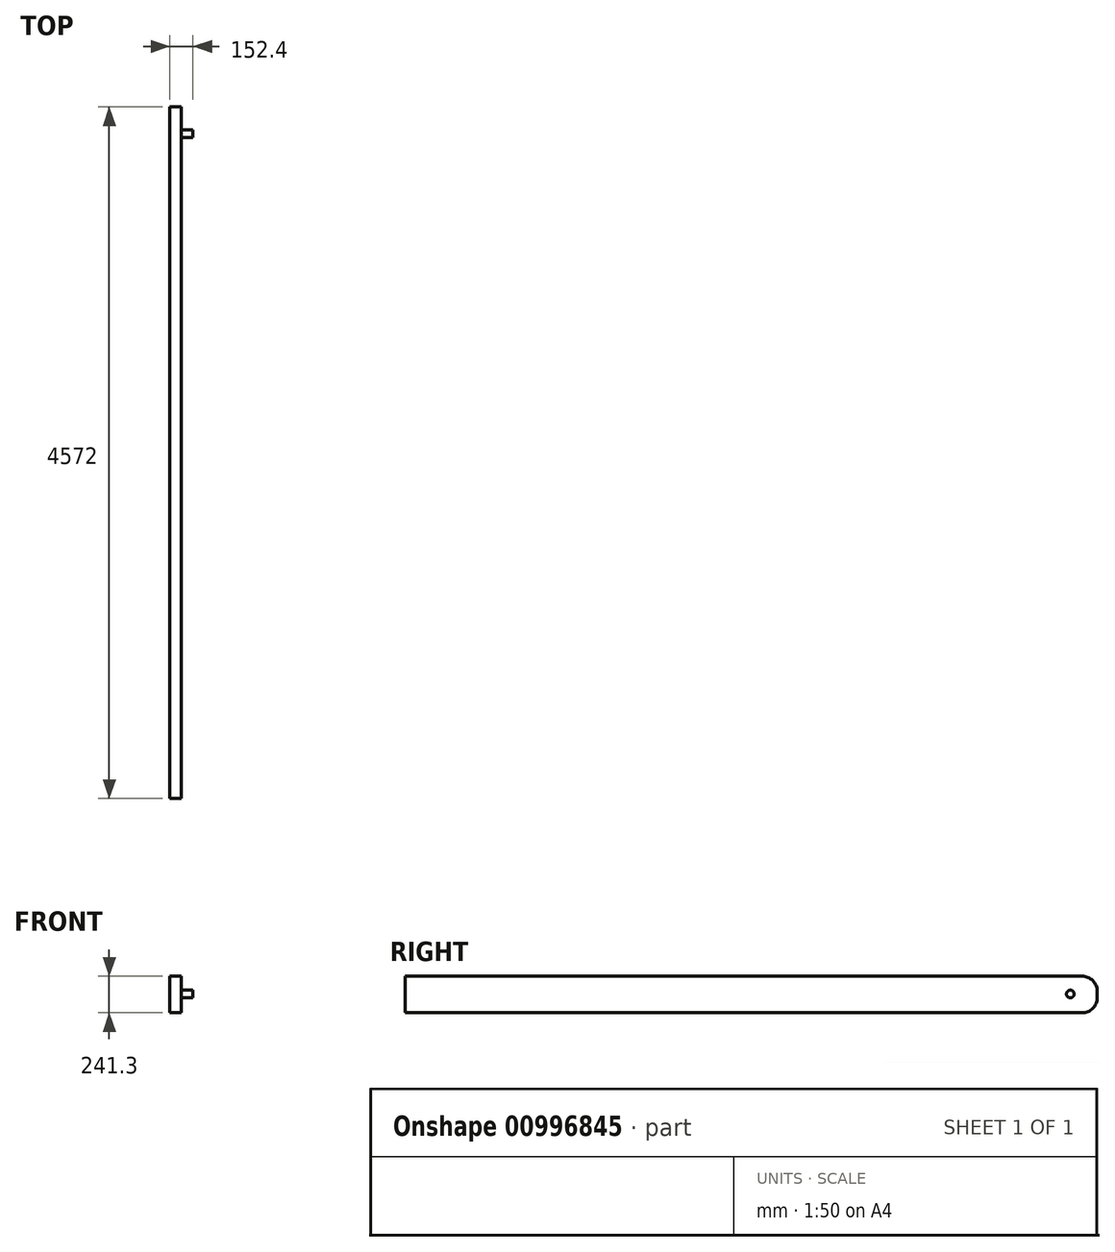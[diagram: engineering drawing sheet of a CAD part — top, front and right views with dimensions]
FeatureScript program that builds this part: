
annotation { "Feature Type Name" : "Feature", "Feature Type Description" : "" }
export const myFeature = defineFeature(function(context is Context, id is Id, definition is map)
    precondition{}
    {
        {
            var Q0;
            Q0=qCreatedBy(makeId("Right.planeOp"),FACE);
            var sketch = newSketch(context, id + "F0", { "sketchPlane" : qUnion([Q0])});
            skLineSegment(sketch, "E0", {"start": v(177.8, 117.22) * mm, "end": v(177.8, -124.08) * mm});
            skLineSegment(sketch, "E1", {"start": v(177.8, 117.22) * mm, "end": v(-4394.2, 117.22) * mm});
            skLineSegment(sketch, "E2", {"start": v(-4394.2, 117.22) * mm, "end": v(-4394.2, -124.08) * mm});
            skLineSegment(sketch, "E3", {"start": v(-4394.2, -124.08) * mm, "end": v(177.8, -124.08) * mm});
            skSolve(sketch);
        }
        {
            var Q0;
            Q0=makeQuery(id+"F0.imprint","IMPRINT",FACE,{"disambiguationData":[TD([[makeQuery(id+"F0.imprint","IMPRINT",EDGE,{"derivedFrom":sQuery(id+"F0.wireOp",EDGE,"E0")}),-1.0]])]});
            extrude(context, id + "F1", {"entities" : qUnion([Q0]), "oppositeDirection" : true, "depth" : 76.2 * mm, "offsetDistance" : 25.4 * mm});
        }
        {
            var Q0;
            Q0=makeQuery(id+"F1.opExtrude","CAP_FACE",FACE,{"disambiguationData":[OSD([sQuery(id+"F0.wireOp",EDGE,"E0"),sQuery(id+"F0.wireOp",EDGE,"E1"),sQuery(id+"F0.wireOp",EDGE,"E2"),sQuery(id+"F0.wireOp",EDGE,"E3")])],"isStart":true});
            var sketch = newSketch(context, id + "F2", { "sketchPlane" : qUnion([Q0])});
            skCircle(sketch, "E4", {"center": v(0, 0) * mm, "radius": 25.4 * mm});
            skSolve(sketch);
        }
        {
            var Q0;
            Q0 = qSketchRegion(id + "F2", true);
            extrude(context, id + "F3", {"entities" : qUnion([Q0]), "operationType" : NewBodyOperationType.ADD, "depth" : 76.2 * mm, "offsetDistance" : 25.4 * mm});
        }
        {
            var Q0;
            Q0=makeQuery(id+"F1.opExtrude","SWEPT_EDGE",EDGE,{"disambiguationData":[OSD([sQuery(id+"F0.wireOp",EDGE,"E0"),sQuery(id+"F0.wireOp",EDGE,"E1")])]});
            var Q1;
            Q1=makeQuery(id+"F1.opExtrude","SWEPT_EDGE",EDGE,{"disambiguationData":[OSD([sQuery(id+"F0.wireOp",EDGE,"E0"),sQuery(id+"F0.wireOp",EDGE,"E3")])]});
            fillet(context, id + "F4", {"entities" : qUnion([Q0, Q1]), "radius" : 99.06 * mm, "tangentPropagation" : true, "allowEdgeOverflow" : false});
        }
    });
